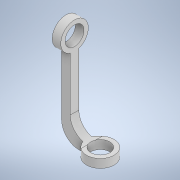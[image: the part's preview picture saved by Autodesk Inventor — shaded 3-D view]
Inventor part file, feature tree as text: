
AUTODESK INVENTOR PART (.ipt)
format: ipt  version: 2022 (Build 260153000, 153)  size: 159,232 bytes
history: native  units: mm
features: extrude x6, sketch x6, other x1, fillet x1
ambient origin geometry x8: Origin, YZ Plane, XZ Plane, XY Plane, X Axis, Y Axis, Z Axis, Center Point
bodies: Body1 (feature_tree)
feature tree (14):
  other  "Bryła1"
  extrude  "Wyciągnięcie proste1"  Depth=22.0mm
  extrude  "Wyciągnięcie proste2"  Depth=5.0mm
  fillet  "Zaokrąglenie1"  Radius=10.0mm
  extrude  "Wyciągnięcie proste3"  Depth=107.5mm
  extrude  "Wyciągnięcie proste4"  Depth=30.0mm
  extrude  "Wyciągnięcie proste5"  Depth=10.0mm
  extrude  "Wyciągnięcie proste6"  Depth=10.0mm
  sketch  "Szkic2"
  sketch  "Szkic4"
  sketch  "Szkic7"
  sketch  "Szkic8"
  sketch  "Szkic9"
  sketch  "Szkic11"
